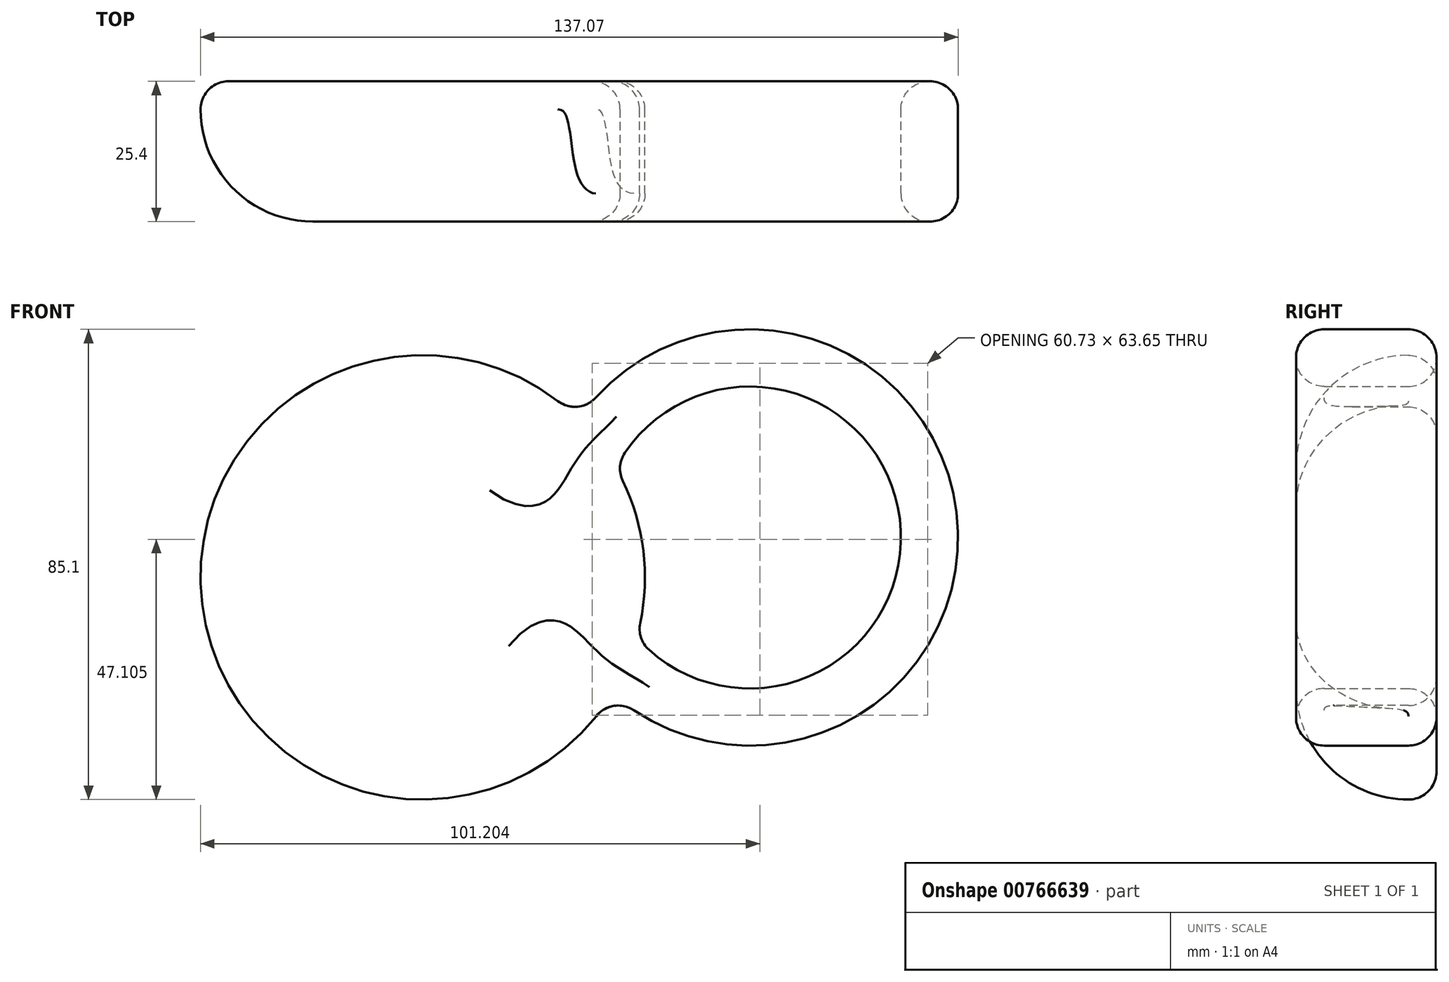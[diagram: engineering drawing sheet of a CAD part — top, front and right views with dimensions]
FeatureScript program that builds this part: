
annotation { "Feature Type Name" : "Feature", "Feature Type Description" : "" }
export const myFeature = defineFeature(function(context is Context, id is Id, definition is map)
    precondition{}
    {
        {
            var Q0;
            Q0=qCreatedBy(makeId("Front.planeOp"),FACE);
            var sketch = newSketch(context, id + "F0", { "sketchPlane" : qUnion([Q0])});
            skCircle(sketch, "E0", {"center": v(-101.84, 40.23) * mm, "radius": 40.2 * mm});
            skSolve(sketch);
        }
        {
            var Q0;
            Q0 = qSketchRegion(id + "F0", true);
            extrude(context, id + "F1", {"entities" : qUnion([Q0]), "depth" : 25.4 * mm, "offsetDistance" : 25.4 * mm});
        }
        {
            var Q0;
            Q0=qCreatedBy(makeId("Front.planeOp"),FACE);
            var sketch = newSketch(context, id + "F2", { "sketchPlane" : qUnion([Q0])});
            skCircle(sketch, "E1", {"center": v(-42.64, 47.45) * mm, "radius": 37.67 * mm});
            skCircle(sketch, "E2", {"center": v(-42.64, 47.45) * mm, "radius": 27.33 * mm});
            skSolve(sketch);
        }
        {
            var Q0;
            Q0 = qSketchRegion(id + "F2", true);
            extrude(context, id + "F3", {"entities" : qUnion([Q0]), "operationType" : NewBodyOperationType.ADD, "depth" : 25.4 * mm, "offsetDistance" : 25.4 * mm});
        }
        {
            var Q0;
            Q0=makeQuery(id+"F3.opExtrude","CAP_EDGE",EDGE,{"disambiguationData":[OSD([sQuery(id+"F2.wireOp",EDGE,"E1")])],"isStart":false});
            var Q1;
            Q1=makeQuery(id+"F3.opExtrude","CAP_EDGE",EDGE,{"disambiguationData":[OSD([sQuery(id+"F2.wireOp",EDGE,"E2")])],"isStart":false});
            fillet(context, id + "F4", {"entities" : qUnion([Q0, Q1]), "radius" : 5.08 * mm, "tangentPropagation" : true, "allowEdgeOverflow" : false});
        }
        {
            var Q0;
            {var subQ0=sQuery(id+"F2.wireOp",EDGE,"E2");var subQ2=sQuery(id+"F0.wireOp",EDGE,"E0");Q0=makeQuery(id+"F3.boolean.opBoolean","SPLIT",FACE,{"disambiguationData":[TD([makeQuery(id+"F3.opExtrude","SWEPT_FACE",FACE,{"disambiguationData":[OSD([subQ0])]})])],"derivedFrom":makeQuery(id+"F1.opExtrude","SWEPT_FACE",FACE,{"disambiguationData":[OSD([subQ2])]})});}
            var Q1;
            Q1=makeQuery(id+"F3.boolean.opBoolean","INTERSECT",EDGE,{"disambiguationData":[OD(0.0)],"derivedFrom":[makeQuery(id+"F1.opExtrude","SWEPT_FACE",FACE,{"disambiguationData":[OSD([sQuery(id+"F0.wireOp",EDGE,"E0")])]}),makeQuery(id+"F3.opExtrude","SWEPT_FACE",FACE,{"disambiguationData":[OSD([sQuery(id+"F2.wireOp",EDGE,"E1")])]})]});
            var Q2;
            Q2=makeQuery(id+"F3.boolean.opBoolean","INTERSECT",EDGE,{"disambiguationData":[OD(1.0)],"derivedFrom":[makeQuery(id+"F1.opExtrude","SWEPT_FACE",FACE,{"disambiguationData":[OSD([sQuery(id+"F0.wireOp",EDGE,"E0")])]}),makeQuery(id+"F3.opExtrude","SWEPT_FACE",FACE,{"disambiguationData":[OSD([sQuery(id+"F2.wireOp",EDGE,"E1")])]})]});
            fillet(context, id + "F5", {"entities" : qUnion([Q0, Q1, Q2]), "radius" : 5.08 * mm, "tangentPropagation" : true, "allowEdgeOverflow" : false});
        }
        {
            var Q0;
            Q0=makeQuery(id+"F3.boolean.opBoolean","MERGE",FACE,{"derivedFrom":[makeQuery(id+"F1.opExtrude","CAP_FACE",FACE,{"disambiguationData":[OSD([sQuery(id+"F0.wireOp",EDGE,"E0")])],"isStart":true}),makeQuery(id+"F3.opExtrude","CAP_FACE",FACE,{"disambiguationData":[OSD([sQuery(id+"F2.wireOp",EDGE,"E1"),sQuery(id+"F2.wireOp",EDGE,"E2")])],"isStart":true})]});
            fillet(context, id + "F6", {"entities" : qUnion([Q0]), "radius" : 5.08 * mm, "tangentPropagation" : true, "allowEdgeOverflow" : false});
        }
        {
            var Q0;
            Q0=makeQuery(id+"F3.boolean.opBoolean","MERGE",FACE,{"derivedFrom":[makeQuery(id+"F1.opExtrude","CAP_FACE",FACE,{"disambiguationData":[OSD([sQuery(id+"F0.wireOp",EDGE,"E0")])],"isStart":false}),makeQuery(id+"F3.opExtrude","CAP_FACE",FACE,{"disambiguationData":[OSD([sQuery(id+"F2.wireOp",EDGE,"E1"),sQuery(id+"F2.wireOp",EDGE,"E2")])],"isStart":false})]});
            var Q1;
            {var subQ0=sQuery(id+"F0.wireOp",EDGE,"E0");var subQ1=makeQuery(id+"F1.opExtrude","SWEPT_FACE",FACE,{"disambiguationData":[OSD([subQ0])]});var subQ2=sQuery(id+"F2.wireOp",EDGE,"E2");var subQ3=makeQuery(id+"F3.opExtrude","SWEPT_FACE",FACE,{"disambiguationData":[OSD([subQ2])]});Q1=makeQuery(id+"F5.opFillet","BLEND_EDGE",EDGE,{"blendedFrom":[makeQuery(id+"F3.boolean.opBoolean","INTERSECT",VERTEX,{"disambiguationData":[OD(0.0)],"derivedFrom":[subQ1,subQ3]}),makeQuery(id+"F3.boolean.opBoolean","SPLIT",EDGE,{"disambiguationData":[TD([subQ3])],"derivedFrom":makeQuery(id+"F1.opExtrude","CAP_EDGE",EDGE,{"disambiguationData":[OSD([subQ0])],"isStart":true})})],"blendedInto":[]});}
            var Q2;
            {var subQ0=sQuery(id+"F2.wireOp",EDGE,"E2");var subQ1=sQuery(id+"F0.wireOp",EDGE,"E0");Q2=makeQuery(id+"F5.opFillet","BLEND_EDGE",EDGE,{"blendedFrom":[makeQuery(id+"F3.boolean.opBoolean","INTERSECT",VERTEX,{"disambiguationData":[OD(0.0)],"derivedFrom":[makeQuery(id+"F1.opExtrude","SWEPT_FACE",FACE,{"disambiguationData":[OSD([subQ1])]}),makeQuery(id+"F3.opExtrude","SWEPT_FACE",FACE,{"disambiguationData":[OSD([subQ0])]})]}),makeQuery(id+"F3.boolean.opBoolean","MERGE",FACE,{"derivedFrom":[makeQuery(id+"F1.opExtrude","CAP_FACE",FACE,{"disambiguationData":[OSD([subQ1])],"isStart":true}),makeQuery(id+"F3.opExtrude","CAP_FACE",FACE,{"disambiguationData":[OSD([sQuery(id+"F2.wireOp",EDGE,"E1"),subQ0])],"isStart":true})]})],"blendedInto":[makeQuery(id+"F3.boolean.opBoolean","MERGE",FACE,{"derivedFrom":[makeQuery(id+"F1.opExtrude","CAP_FACE",FACE,{"disambiguationData":[OSD([subQ1])],"isStart":true}),makeQuery(id+"F3.opExtrude","CAP_FACE",FACE,{"disambiguationData":[OSD([sQuery(id+"F2.wireOp",EDGE,"E1"),subQ0])],"isStart":true})]})]});}
            var Q3;
            {var subQ0=makeQuery(id+"F3.opExtrude","SWEPT_FACE",FACE,{"disambiguationData":[OSD([sQuery(id+"F2.wireOp",EDGE,"E2")])]});var subQ1=makeQuery(id+"F1.opExtrude","SWEPT_FACE",FACE,{"disambiguationData":[OSD([sQuery(id+"F0.wireOp",EDGE,"E0")])]});Q3=makeQuery(id+"F5.opFillet","BLEND_EDGE",EDGE,{"blendedFrom":[makeQuery(id+"F3.boolean.opBoolean","INTERSECT",VERTEX,{"disambiguationData":[OD(0.0)],"derivedFrom":[subQ1,subQ0]}),makeQuery(id+"F3.boolean.opBoolean","INTERSECT",EDGE,{"disambiguationData":[OD(0.0)],"derivedFrom":[subQ1,subQ0]})],"blendedInto":[]});}
            var Q4;
            {var subQ0=sQuery(id+"F2.wireOp",EDGE,"E1");var subQ1=makeQuery(id+"F3.opExtrude","CAP_FACE",FACE,{"disambiguationData":[OSD([subQ0,sQuery(id+"F2.wireOp",EDGE,"E2")])],"isStart":true});var subQ2=sQuery(id+"F0.wireOp",EDGE,"E0");var subQ3=makeQuery(id+"F1.opExtrude","CAP_FACE",FACE,{"disambiguationData":[OSD([subQ2])],"isStart":true});var subQ4=makeQuery(id+"F3.opExtrude","SWEPT_FACE",FACE,{"disambiguationData":[OSD([subQ0])]});var subQ5=makeQuery(id+"F1.opExtrude","SWEPT_FACE",FACE,{"disambiguationData":[OSD([subQ2])]});Q4=makeQuery(id+"F6.opFillet","BLEND_EDGE",EDGE,{"blendedFrom":[makeQuery(id+"F3.boolean.opBoolean","SPLIT",EDGE,{"disambiguationData":[TD([subQ4])],"derivedFrom":makeQuery(id+"F1.opExtrude","CAP_EDGE",EDGE,{"disambiguationData":[OSD([subQ2])],"isStart":true})}),makeQuery(id+"F5.opFillet","BLEND_EDGE",EDGE,{"blendedFrom":[makeQuery(id+"F3.boolean.opBoolean","INTERSECT",EDGE,{"disambiguationData":[OD(0.0)],"derivedFrom":[subQ5,subQ4]}),makeQuery(id+"F3.boolean.opBoolean","MERGE",FACE,{"derivedFrom":[subQ3,subQ1]})],"blendedInto":[makeQuery(id+"F3.boolean.opBoolean","MERGE",FACE,{"derivedFrom":[subQ3,subQ1]})]})],"blendedInto":[]});}
            var Q5;
            {var subQ0=sQuery(id+"F2.wireOp",EDGE,"E2");Q5=makeQuery(id+"F5.opFillet","BLEND_EDGE",EDGE,{"blendedFrom":[makeQuery(id+"F3.boolean.opBoolean","INTERSECT",VERTEX,{"disambiguationData":[OD(0.0)],"derivedFrom":[makeQuery(id+"F1.opExtrude","SWEPT_FACE",FACE,{"disambiguationData":[OSD([sQuery(id+"F0.wireOp",EDGE,"E0")])]}),makeQuery(id+"F3.opExtrude","SWEPT_FACE",FACE,{"disambiguationData":[OSD([subQ0])]})]}),makeQuery(id+"F3.opExtrude","CAP_EDGE",EDGE,{"disambiguationData":[OSD([subQ0])],"isStart":true})],"blendedInto":[]});}
            var Q6;
            {var subQ0=makeQuery(id+"F3.opExtrude","SWEPT_FACE",FACE,{"disambiguationData":[OSD([sQuery(id+"F2.wireOp",EDGE,"E1")])]});Q6=makeQuery(id+"F5.opFillet","BLEND_EDGE",EDGE,{"blendedFrom":[makeQuery(id+"F3.boolean.opBoolean","INTERSECT",EDGE,{"disambiguationData":[OD(1.0)],"derivedFrom":[makeQuery(id+"F1.opExtrude","SWEPT_FACE",FACE,{"disambiguationData":[OSD([sQuery(id+"F0.wireOp",EDGE,"E0")])]}),subQ0]}),subQ0],"blendedInto":[subQ0]});}
            var Q7;
            {var subQ0=makeQuery(id+"F3.opExtrude","SWEPT_FACE",FACE,{"disambiguationData":[OSD([sQuery(id+"F2.wireOp",EDGE,"E1")])]});Q7=makeQuery(id+"F5.opFillet","BLEND_EDGE",EDGE,{"blendedFrom":[makeQuery(id+"F3.boolean.opBoolean","INTERSECT",EDGE,{"disambiguationData":[OD(0.0)],"derivedFrom":[makeQuery(id+"F1.opExtrude","SWEPT_FACE",FACE,{"disambiguationData":[OSD([sQuery(id+"F0.wireOp",EDGE,"E0")])]}),subQ0]}),subQ0],"blendedInto":[subQ0]});}
            var Q8;
            {var subQ0=sQuery(id+"F2.wireOp",EDGE,"E2");var subQ3=sQuery(id+"F0.wireOp",EDGE,"E0");var subQ5=makeQuery(id+"F3.opExtrude","SWEPT_FACE",FACE,{"disambiguationData":[OSD([subQ0])]});var subQ6=makeQuery(id+"F1.opExtrude","SWEPT_FACE",FACE,{"disambiguationData":[OSD([subQ3])]});Q8=makeQuery(id+"F5.opFillet","BLEND_EDGE",EDGE,{"blendedFrom":[makeQuery(id+"F3.boolean.opBoolean","SPLIT",EDGE,{"disambiguationData":[TD([subQ5])],"derivedFrom":makeQuery(id+"F1.opExtrude","CAP_EDGE",EDGE,{"disambiguationData":[OSD([subQ3])],"isStart":true})}),makeQuery(id+"F3.boolean.opBoolean","SPLIT",FACE,{"disambiguationData":[TD([subQ5])],"derivedFrom":subQ6})],"blendedInto":[makeQuery(id+"F3.boolean.opBoolean","SPLIT",FACE,{"disambiguationData":[TD([subQ5])],"derivedFrom":subQ6})]});}
            var Q9;
            {var subQ0=sQuery(id+"F2.wireOp",EDGE,"E2");var subQ1=makeQuery(id+"F3.opExtrude","CAP_FACE",FACE,{"disambiguationData":[OSD([sQuery(id+"F2.wireOp",EDGE,"E1"),subQ0])],"isStart":true});var subQ2=sQuery(id+"F0.wireOp",EDGE,"E0");var subQ3=makeQuery(id+"F1.opExtrude","CAP_FACE",FACE,{"disambiguationData":[OSD([subQ2])],"isStart":true});Q9=makeQuery(id+"F5.opFillet","BLEND_EDGE",EDGE,{"blendedFrom":[makeQuery(id+"F3.boolean.opBoolean","SPLIT",EDGE,{"disambiguationData":[TD([makeQuery(id+"F3.opExtrude","SWEPT_FACE",FACE,{"disambiguationData":[OSD([subQ0])]})])],"derivedFrom":makeQuery(id+"F1.opExtrude","CAP_EDGE",EDGE,{"disambiguationData":[OSD([subQ2])],"isStart":true})}),makeQuery(id+"F3.boolean.opBoolean","MERGE",FACE,{"derivedFrom":[subQ3,subQ1]})],"blendedInto":[makeQuery(id+"F3.boolean.opBoolean","MERGE",FACE,{"derivedFrom":[subQ3,subQ1]})]});}
            var Q10;
            {var subQ0=sQuery(id+"F2.wireOp",EDGE,"E2");var subQ1=makeQuery(id+"F3.opExtrude","CAP_FACE",FACE,{"disambiguationData":[OSD([sQuery(id+"F2.wireOp",EDGE,"E1"),subQ0])],"isStart":false});var subQ2=sQuery(id+"F0.wireOp",EDGE,"E0");var subQ3=makeQuery(id+"F1.opExtrude","CAP_FACE",FACE,{"disambiguationData":[OSD([subQ2])],"isStart":false});Q10=makeQuery(id+"F5.opFillet","BLEND_EDGE",EDGE,{"blendedFrom":[makeQuery(id+"F3.boolean.opBoolean","SPLIT",EDGE,{"disambiguationData":[TD([makeQuery(id+"F3.opExtrude","SWEPT_FACE",FACE,{"disambiguationData":[OSD([subQ0])]})])],"derivedFrom":makeQuery(id+"F1.opExtrude","CAP_EDGE",EDGE,{"disambiguationData":[OSD([subQ2])],"isStart":false})}),makeQuery(id+"F3.boolean.opBoolean","MERGE",FACE,{"derivedFrom":[subQ3,subQ1]})],"blendedInto":[makeQuery(id+"F3.boolean.opBoolean","MERGE",FACE,{"derivedFrom":[subQ3,subQ1]})]});}
            var Q11;
            {var subQ0=sQuery(id+"F2.wireOp",EDGE,"E2");var subQ2=sQuery(id+"F0.wireOp",EDGE,"E0");Q11=makeQuery(id+"F5.opFillet","BLEND_EDGE",EDGE,{"blendedFrom":[makeQuery(id+"F4.opFillet","BLEND_EDGE",EDGE,{"disambiguationData":[OD(1.0)],"blendedFrom":[makeQuery(id+"F3.opExtrude","CAP_EDGE",EDGE,{"disambiguationData":[OSD([subQ0])],"isStart":false}),makeQuery(id+"F3.boolean.opBoolean","SPLIT",FACE,{"disambiguationData":[TD([makeQuery(id+"F3.opExtrude","SWEPT_FACE",FACE,{"disambiguationData":[OSD([subQ0])]})])],"derivedFrom":makeQuery(id+"F1.opExtrude","SWEPT_FACE",FACE,{"disambiguationData":[OSD([subQ2])]})})],"blendedInto":[makeQuery(id+"F3.boolean.opBoolean","SPLIT",FACE,{"disambiguationData":[TD([makeQuery(id+"F3.opExtrude","SWEPT_FACE",FACE,{"disambiguationData":[OSD([subQ0])]})])],"derivedFrom":makeQuery(id+"F1.opExtrude","SWEPT_FACE",FACE,{"disambiguationData":[OSD([subQ2])]})})]}),makeQuery(id+"F4.opFillet","BLEND_FACE",FACE,{"disambiguationData":[OSD([subQ0])]})],"blendedInto":[makeQuery(id+"F4.opFillet","BLEND_FACE",FACE,{"disambiguationData":[OSD([subQ0])]})]});}
            var Q12;
            {var subQ0=sQuery(id+"F2.wireOp",EDGE,"E2");var subQ3=sQuery(id+"F0.wireOp",EDGE,"E0");var subQ5=makeQuery(id+"F3.opExtrude","SWEPT_FACE",FACE,{"disambiguationData":[OSD([subQ0])]});var subQ6=makeQuery(id+"F1.opExtrude","SWEPT_FACE",FACE,{"disambiguationData":[OSD([subQ3])]});Q12=makeQuery(id+"F5.opFillet","BLEND_EDGE",EDGE,{"blendedFrom":[makeQuery(id+"F3.boolean.opBoolean","SPLIT",EDGE,{"disambiguationData":[TD([subQ5])],"derivedFrom":makeQuery(id+"F1.opExtrude","CAP_EDGE",EDGE,{"disambiguationData":[OSD([subQ3])],"isStart":false})}),makeQuery(id+"F3.boolean.opBoolean","SPLIT",FACE,{"disambiguationData":[TD([subQ5])],"derivedFrom":subQ6})],"blendedInto":[makeQuery(id+"F3.boolean.opBoolean","SPLIT",FACE,{"disambiguationData":[TD([subQ5])],"derivedFrom":subQ6})]});}
            var Q13;
            {var subQ0=sQuery(id+"F2.wireOp",EDGE,"E2");var subQ1=sQuery(id+"F2.wireOp",EDGE,"E1");var subQ2=makeQuery(id+"F3.opExtrude","CAP_FACE",FACE,{"disambiguationData":[OSD([subQ1,subQ0])],"isStart":false});var subQ3=sQuery(id+"F0.wireOp",EDGE,"E0");var subQ4=makeQuery(id+"F1.opExtrude","CAP_FACE",FACE,{"disambiguationData":[OSD([subQ3])],"isStart":false});Q13=makeQuery(id+"F5.opFillet","BLEND_EDGE",EDGE,{"blendedFrom":[makeQuery(id+"F4.opFillet","BLEND_EDGE",EDGE,{"disambiguationData":[OD(1.0)],"blendedFrom":[makeQuery(id+"F3.opExtrude","CAP_EDGE",EDGE,{"disambiguationData":[OSD([subQ0])],"isStart":false}),makeQuery(id+"F3.boolean.opBoolean","SPLIT",FACE,{"disambiguationData":[TD([makeQuery(id+"F3.opExtrude","SWEPT_FACE",FACE,{"disambiguationData":[OSD([subQ0])]})])],"derivedFrom":makeQuery(id+"F1.opExtrude","SWEPT_FACE",FACE,{"disambiguationData":[OSD([subQ3])]})})],"blendedInto":[makeQuery(id+"F3.boolean.opBoolean","SPLIT",FACE,{"disambiguationData":[TD([makeQuery(id+"F3.opExtrude","SWEPT_FACE",FACE,{"disambiguationData":[OSD([subQ0])]})])],"derivedFrom":makeQuery(id+"F1.opExtrude","SWEPT_FACE",FACE,{"disambiguationData":[OSD([subQ3])]})})]}),makeQuery(id+"F3.boolean.opBoolean","MERGE",FACE,{"derivedFrom":[subQ4,subQ2]})],"blendedInto":[makeQuery(id+"F3.boolean.opBoolean","MERGE",FACE,{"derivedFrom":[subQ4,subQ2]})]});}
            var Q14;
            {var subQ1=sQuery(id+"F2.wireOp",EDGE,"E1");var subQ2=sQuery(id+"F0.wireOp",EDGE,"E0");var subQ3=makeQuery(id+"F3.opExtrude","SWEPT_FACE",FACE,{"disambiguationData":[OSD([subQ1])]});var subQ4=makeQuery(id+"F1.opExtrude","SWEPT_FACE",FACE,{"disambiguationData":[OSD([subQ2])]});Q14=makeQuery(id+"F5.opFillet","BLEND_EDGE",EDGE,{"blendedFrom":[makeQuery(id+"F3.boolean.opBoolean","INTERSECT",EDGE,{"disambiguationData":[OD(1.0)],"derivedFrom":[subQ4,subQ3]}),makeQuery(id+"F4.opFillet","BLEND_EDGE",EDGE,{"disambiguationData":[OD(1.0)],"blendedFrom":[makeQuery(id+"F3.opExtrude","CAP_EDGE",EDGE,{"disambiguationData":[OSD([subQ1])],"isStart":false}),makeQuery(id+"F3.boolean.opBoolean","SPLIT",FACE,{"disambiguationData":[TD([subQ3])],"derivedFrom":subQ4})],"blendedInto":[makeQuery(id+"F3.boolean.opBoolean","SPLIT",FACE,{"disambiguationData":[TD([subQ3])],"derivedFrom":subQ4})]})],"blendedInto":[]});}
            var Q15;
            {var subQ0=sQuery(id+"F2.wireOp",EDGE,"E1");var subQ1=sQuery(id+"F0.wireOp",EDGE,"E0");Q15=makeQuery(id+"F6.opFillet","BLEND_EDGE",EDGE,{"blendedFrom":[makeQuery(id+"F3.opExtrude","CAP_EDGE",EDGE,{"disambiguationData":[OSD([subQ0])],"isStart":true}),makeQuery(id+"F5.opFillet","BLEND_EDGE",EDGE,{"blendedFrom":[makeQuery(id+"F3.boolean.opBoolean","INTERSECT",EDGE,{"disambiguationData":[OD(1.0)],"derivedFrom":[makeQuery(id+"F1.opExtrude","SWEPT_FACE",FACE,{"disambiguationData":[OSD([subQ1])]}),makeQuery(id+"F3.opExtrude","SWEPT_FACE",FACE,{"disambiguationData":[OSD([subQ0])]})]}),makeQuery(id+"F3.boolean.opBoolean","MERGE",FACE,{"derivedFrom":[makeQuery(id+"F1.opExtrude","CAP_FACE",FACE,{"disambiguationData":[OSD([subQ1])],"isStart":true}),makeQuery(id+"F3.opExtrude","CAP_FACE",FACE,{"disambiguationData":[OSD([subQ0,sQuery(id+"F2.wireOp",EDGE,"E2")])],"isStart":true})]})],"blendedInto":[makeQuery(id+"F3.boolean.opBoolean","MERGE",FACE,{"derivedFrom":[makeQuery(id+"F1.opExtrude","CAP_FACE",FACE,{"disambiguationData":[OSD([subQ1])],"isStart":true}),makeQuery(id+"F3.opExtrude","CAP_FACE",FACE,{"disambiguationData":[OSD([subQ0,sQuery(id+"F2.wireOp",EDGE,"E2")])],"isStart":true})]})]})],"blendedInto":[]});}
            var Q16;
            {var subQ0=sQuery(id+"F2.wireOp",EDGE,"E2");var subQ2=sQuery(id+"F0.wireOp",EDGE,"E0");var subQ3=makeQuery(id+"F3.opExtrude","SWEPT_FACE",FACE,{"disambiguationData":[OSD([subQ0])]});var subQ4=makeQuery(id+"F1.opExtrude","SWEPT_FACE",FACE,{"disambiguationData":[OSD([subQ2])]});Q16=makeQuery(id+"F5.opFillet","BLEND_EDGE",EDGE,{"blendedFrom":[makeQuery(id+"F3.boolean.opBoolean","INTERSECT",EDGE,{"disambiguationData":[OD(1.0)],"derivedFrom":[subQ4,subQ3]}),makeQuery(id+"F4.opFillet","BLEND_EDGE",EDGE,{"disambiguationData":[OD(1.0)],"blendedFrom":[makeQuery(id+"F3.opExtrude","CAP_EDGE",EDGE,{"disambiguationData":[OSD([subQ0])],"isStart":false}),makeQuery(id+"F3.boolean.opBoolean","SPLIT",FACE,{"disambiguationData":[TD([subQ3])],"derivedFrom":subQ4})],"blendedInto":[makeQuery(id+"F3.boolean.opBoolean","SPLIT",FACE,{"disambiguationData":[TD([subQ3])],"derivedFrom":subQ4})]})],"blendedInto":[]});}
            var Q17;
            {var subQ0=makeQuery(id+"F3.opExtrude","SWEPT_FACE",FACE,{"disambiguationData":[OSD([sQuery(id+"F2.wireOp",EDGE,"E2")])]});Q17=makeQuery(id+"F5.opFillet","BLEND_EDGE",EDGE,{"blendedFrom":[makeQuery(id+"F3.boolean.opBoolean","INTERSECT",EDGE,{"disambiguationData":[OD(1.0)],"derivedFrom":[makeQuery(id+"F1.opExtrude","SWEPT_FACE",FACE,{"disambiguationData":[OSD([sQuery(id+"F0.wireOp",EDGE,"E0")])]}),subQ0]}),subQ0],"blendedInto":[subQ0]});}
            var Q18;
            {var subQ1=sQuery(id+"F2.wireOp",EDGE,"E1");var subQ2=sQuery(id+"F0.wireOp",EDGE,"E0");var subQ3=makeQuery(id+"F3.opExtrude","SWEPT_FACE",FACE,{"disambiguationData":[OSD([subQ1])]});var subQ4=makeQuery(id+"F1.opExtrude","SWEPT_FACE",FACE,{"disambiguationData":[OSD([subQ2])]});Q18=makeQuery(id+"F5.opFillet","BLEND_EDGE",EDGE,{"blendedFrom":[makeQuery(id+"F3.boolean.opBoolean","INTERSECT",EDGE,{"disambiguationData":[OD(0.0)],"derivedFrom":[subQ4,subQ3]}),makeQuery(id+"F4.opFillet","BLEND_EDGE",EDGE,{"disambiguationData":[OD(0.0)],"blendedFrom":[makeQuery(id+"F3.opExtrude","CAP_EDGE",EDGE,{"disambiguationData":[OSD([subQ1])],"isStart":false}),makeQuery(id+"F3.boolean.opBoolean","SPLIT",FACE,{"disambiguationData":[TD([subQ3])],"derivedFrom":subQ4})],"blendedInto":[makeQuery(id+"F3.boolean.opBoolean","SPLIT",FACE,{"disambiguationData":[TD([subQ3])],"derivedFrom":subQ4})]})],"blendedInto":[]});}
            var Q19;
            {var subQ0=sQuery(id+"F2.wireOp",EDGE,"E2");var subQ2=sQuery(id+"F0.wireOp",EDGE,"E0");var subQ3=makeQuery(id+"F3.opExtrude","SWEPT_FACE",FACE,{"disambiguationData":[OSD([subQ0])]});var subQ4=makeQuery(id+"F1.opExtrude","SWEPT_FACE",FACE,{"disambiguationData":[OSD([subQ2])]});Q19=makeQuery(id+"F5.opFillet","BLEND_EDGE",EDGE,{"blendedFrom":[makeQuery(id+"F3.boolean.opBoolean","INTERSECT",EDGE,{"disambiguationData":[OD(1.0)],"derivedFrom":[subQ4,subQ3]}),makeQuery(id+"F3.boolean.opBoolean","SPLIT",FACE,{"disambiguationData":[TD([subQ3])],"derivedFrom":subQ4})],"blendedInto":[makeQuery(id+"F3.boolean.opBoolean","SPLIT",FACE,{"disambiguationData":[TD([subQ3])],"derivedFrom":subQ4})]});}
            var Q20;
            {var subQ1=sQuery(id+"F2.wireOp",EDGE,"E1");var subQ2=sQuery(id+"F0.wireOp",EDGE,"E0");var subQ3=makeQuery(id+"F3.opExtrude","SWEPT_FACE",FACE,{"disambiguationData":[OSD([subQ1])]});var subQ4=makeQuery(id+"F1.opExtrude","SWEPT_FACE",FACE,{"disambiguationData":[OSD([subQ2])]});Q20=makeQuery(id+"F5.opFillet","BLEND_EDGE",EDGE,{"blendedFrom":[makeQuery(id+"F3.boolean.opBoolean","INTERSECT",EDGE,{"disambiguationData":[OD(1.0)],"derivedFrom":[subQ4,subQ3]}),makeQuery(id+"F3.boolean.opBoolean","SPLIT",FACE,{"disambiguationData":[TD([subQ3])],"derivedFrom":subQ4})],"blendedInto":[makeQuery(id+"F3.boolean.opBoolean","SPLIT",FACE,{"disambiguationData":[TD([subQ3])],"derivedFrom":subQ4})]});}
            var Q21;
            {var subQ0=sQuery(id+"F2.wireOp",EDGE,"E1");var subQ2=sQuery(id+"F0.wireOp",EDGE,"E0");Q21=makeQuery(id+"F5.opFillet","BLEND_EDGE",EDGE,{"blendedFrom":[makeQuery(id+"F4.opFillet","BLEND_EDGE",EDGE,{"disambiguationData":[OD(0.0)],"blendedFrom":[makeQuery(id+"F3.opExtrude","CAP_EDGE",EDGE,{"disambiguationData":[OSD([subQ0])],"isStart":false}),makeQuery(id+"F3.boolean.opBoolean","SPLIT",FACE,{"disambiguationData":[TD([makeQuery(id+"F3.opExtrude","SWEPT_FACE",FACE,{"disambiguationData":[OSD([subQ0])]})])],"derivedFrom":makeQuery(id+"F1.opExtrude","SWEPT_FACE",FACE,{"disambiguationData":[OSD([subQ2])]})})],"blendedInto":[makeQuery(id+"F3.boolean.opBoolean","SPLIT",FACE,{"disambiguationData":[TD([makeQuery(id+"F3.opExtrude","SWEPT_FACE",FACE,{"disambiguationData":[OSD([subQ0])]})])],"derivedFrom":makeQuery(id+"F1.opExtrude","SWEPT_FACE",FACE,{"disambiguationData":[OSD([subQ2])]})})]}),makeQuery(id+"F4.opFillet","BLEND_FACE",FACE,{"disambiguationData":[OSD([subQ0])]})],"blendedInto":[makeQuery(id+"F4.opFillet","BLEND_FACE",FACE,{"disambiguationData":[OSD([subQ0])]})]});}
            var Q22;
            {var subQ0=sQuery(id+"F2.wireOp",EDGE,"E1");var subQ1=sQuery(id+"F0.wireOp",EDGE,"E0");Q22=makeQuery(id+"F6.opFillet","BLEND_EDGE",EDGE,{"blendedFrom":[makeQuery(id+"F3.opExtrude","CAP_EDGE",EDGE,{"disambiguationData":[OSD([subQ0])],"isStart":true}),makeQuery(id+"F5.opFillet","BLEND_EDGE",EDGE,{"blendedFrom":[makeQuery(id+"F3.boolean.opBoolean","INTERSECT",EDGE,{"disambiguationData":[OD(0.0)],"derivedFrom":[makeQuery(id+"F1.opExtrude","SWEPT_FACE",FACE,{"disambiguationData":[OSD([subQ1])]}),makeQuery(id+"F3.opExtrude","SWEPT_FACE",FACE,{"disambiguationData":[OSD([subQ0])]})]}),makeQuery(id+"F3.boolean.opBoolean","MERGE",FACE,{"derivedFrom":[makeQuery(id+"F1.opExtrude","CAP_FACE",FACE,{"disambiguationData":[OSD([subQ1])],"isStart":true}),makeQuery(id+"F3.opExtrude","CAP_FACE",FACE,{"disambiguationData":[OSD([subQ0,sQuery(id+"F2.wireOp",EDGE,"E2")])],"isStart":true})]})],"blendedInto":[makeQuery(id+"F3.boolean.opBoolean","MERGE",FACE,{"derivedFrom":[makeQuery(id+"F1.opExtrude","CAP_FACE",FACE,{"disambiguationData":[OSD([subQ1])],"isStart":true}),makeQuery(id+"F3.opExtrude","CAP_FACE",FACE,{"disambiguationData":[OSD([subQ0,sQuery(id+"F2.wireOp",EDGE,"E2")])],"isStart":true})]})]})],"blendedInto":[]});}
            var Q23;
            {var subQ0=sQuery(id+"F2.wireOp",EDGE,"E2");var subQ1=sQuery(id+"F2.wireOp",EDGE,"E1");var subQ2=makeQuery(id+"F3.opExtrude","CAP_FACE",FACE,{"disambiguationData":[OSD([subQ1,subQ0])],"isStart":false});var subQ3=sQuery(id+"F0.wireOp",EDGE,"E0");var subQ4=makeQuery(id+"F1.opExtrude","CAP_FACE",FACE,{"disambiguationData":[OSD([subQ3])],"isStart":false});Q23=makeQuery(id+"F5.opFillet","BLEND_EDGE",EDGE,{"blendedFrom":[makeQuery(id+"F4.opFillet","BLEND_EDGE",EDGE,{"disambiguationData":[OD(0.0)],"blendedFrom":[makeQuery(id+"F3.opExtrude","CAP_EDGE",EDGE,{"disambiguationData":[OSD([subQ1])],"isStart":false}),makeQuery(id+"F3.boolean.opBoolean","SPLIT",FACE,{"disambiguationData":[TD([makeQuery(id+"F3.opExtrude","SWEPT_FACE",FACE,{"disambiguationData":[OSD([subQ1])]})])],"derivedFrom":makeQuery(id+"F1.opExtrude","SWEPT_FACE",FACE,{"disambiguationData":[OSD([subQ3])]})})],"blendedInto":[makeQuery(id+"F3.boolean.opBoolean","SPLIT",FACE,{"disambiguationData":[TD([makeQuery(id+"F3.opExtrude","SWEPT_FACE",FACE,{"disambiguationData":[OSD([subQ1])]})])],"derivedFrom":makeQuery(id+"F1.opExtrude","SWEPT_FACE",FACE,{"disambiguationData":[OSD([subQ3])]})})]}),makeQuery(id+"F3.boolean.opBoolean","MERGE",FACE,{"derivedFrom":[subQ4,subQ2]})],"blendedInto":[makeQuery(id+"F3.boolean.opBoolean","MERGE",FACE,{"derivedFrom":[subQ4,subQ2]})]});}
            var Q24;
            {var subQ0=sQuery(id+"F2.wireOp",EDGE,"E2");var subQ2=sQuery(id+"F0.wireOp",EDGE,"E0");var subQ3=makeQuery(id+"F3.opExtrude","SWEPT_FACE",FACE,{"disambiguationData":[OSD([subQ0])]});var subQ4=makeQuery(id+"F1.opExtrude","SWEPT_FACE",FACE,{"disambiguationData":[OSD([subQ2])]});Q24=makeQuery(id+"F5.opFillet","BLEND_EDGE",EDGE,{"blendedFrom":[makeQuery(id+"F3.boolean.opBoolean","INTERSECT",EDGE,{"disambiguationData":[OD(0.0)],"derivedFrom":[subQ4,subQ3]}),makeQuery(id+"F4.opFillet","BLEND_EDGE",EDGE,{"disambiguationData":[OD(0.0)],"blendedFrom":[makeQuery(id+"F3.opExtrude","CAP_EDGE",EDGE,{"disambiguationData":[OSD([subQ0])],"isStart":false}),makeQuery(id+"F3.boolean.opBoolean","SPLIT",FACE,{"disambiguationData":[TD([subQ3])],"derivedFrom":subQ4})],"blendedInto":[makeQuery(id+"F3.boolean.opBoolean","SPLIT",FACE,{"disambiguationData":[TD([subQ3])],"derivedFrom":subQ4})]})],"blendedInto":[]});}
            var Q25;
            {var subQ1=sQuery(id+"F2.wireOp",EDGE,"E1");var subQ2=sQuery(id+"F0.wireOp",EDGE,"E0");var subQ3=makeQuery(id+"F3.boolean.opBoolean","SPLIT",FACE,{"disambiguationData":[TD([makeQuery(id+"F3.opExtrude","SWEPT_FACE",FACE,{"disambiguationData":[OSD([subQ1])]})])],"derivedFrom":makeQuery(id+"F1.opExtrude","SWEPT_FACE",FACE,{"disambiguationData":[OSD([subQ2])]})});Q25=makeQuery(id+"F5.opFillet","BLEND_EDGE",EDGE,{"blendedFrom":[makeQuery(id+"F4.opFillet","BLEND_EDGE",EDGE,{"disambiguationData":[OD(0.0)],"blendedFrom":[makeQuery(id+"F3.opExtrude","CAP_EDGE",EDGE,{"disambiguationData":[OSD([subQ1])],"isStart":false}),subQ3],"blendedInto":[subQ3]}),subQ3],"blendedInto":[subQ3]});}
            var Q26;
            {var subQ0=makeQuery(id+"F3.opExtrude","SWEPT_FACE",FACE,{"disambiguationData":[OSD([sQuery(id+"F2.wireOp",EDGE,"E2")])]});Q26=makeQuery(id+"F5.opFillet","BLEND_EDGE",EDGE,{"blendedFrom":[makeQuery(id+"F3.boolean.opBoolean","INTERSECT",EDGE,{"disambiguationData":[OD(0.0)],"derivedFrom":[makeQuery(id+"F1.opExtrude","SWEPT_FACE",FACE,{"disambiguationData":[OSD([sQuery(id+"F0.wireOp",EDGE,"E0")])]}),subQ0]}),subQ0],"blendedInto":[subQ0]});}
            var Q27;
            {var subQ0=sQuery(id+"F2.wireOp",EDGE,"E1");var subQ2=sQuery(id+"F0.wireOp",EDGE,"E0");Q27=makeQuery(id+"F5.opFillet","BLEND_EDGE",EDGE,{"blendedFrom":[makeQuery(id+"F4.opFillet","BLEND_EDGE",EDGE,{"disambiguationData":[OD(1.0)],"blendedFrom":[makeQuery(id+"F3.opExtrude","CAP_EDGE",EDGE,{"disambiguationData":[OSD([subQ0])],"isStart":false}),makeQuery(id+"F3.boolean.opBoolean","SPLIT",FACE,{"disambiguationData":[TD([makeQuery(id+"F3.opExtrude","SWEPT_FACE",FACE,{"disambiguationData":[OSD([subQ0])]})])],"derivedFrom":makeQuery(id+"F1.opExtrude","SWEPT_FACE",FACE,{"disambiguationData":[OSD([subQ2])]})})],"blendedInto":[makeQuery(id+"F3.boolean.opBoolean","SPLIT",FACE,{"disambiguationData":[TD([makeQuery(id+"F3.opExtrude","SWEPT_FACE",FACE,{"disambiguationData":[OSD([subQ0])]})])],"derivedFrom":makeQuery(id+"F1.opExtrude","SWEPT_FACE",FACE,{"disambiguationData":[OSD([subQ2])]})})]}),makeQuery(id+"F4.opFillet","BLEND_FACE",FACE,{"disambiguationData":[OSD([subQ0])]})],"blendedInto":[makeQuery(id+"F4.opFillet","BLEND_FACE",FACE,{"disambiguationData":[OSD([subQ0])]})]});}
            var Q28;
            {var subQ0=sQuery(id+"F2.wireOp",EDGE,"E2");var subQ2=sQuery(id+"F0.wireOp",EDGE,"E0");var subQ3=makeQuery(id+"F3.opExtrude","SWEPT_FACE",FACE,{"disambiguationData":[OSD([subQ0])]});var subQ4=makeQuery(id+"F1.opExtrude","SWEPT_FACE",FACE,{"disambiguationData":[OSD([subQ2])]});Q28=makeQuery(id+"F5.opFillet","BLEND_EDGE",EDGE,{"blendedFrom":[makeQuery(id+"F3.boolean.opBoolean","INTERSECT",EDGE,{"disambiguationData":[OD(0.0)],"derivedFrom":[subQ4,subQ3]}),makeQuery(id+"F3.boolean.opBoolean","SPLIT",FACE,{"disambiguationData":[TD([subQ3])],"derivedFrom":subQ4})],"blendedInto":[makeQuery(id+"F3.boolean.opBoolean","SPLIT",FACE,{"disambiguationData":[TD([subQ3])],"derivedFrom":subQ4})]});}
            var Q29;
            {var subQ0=sQuery(id+"F2.wireOp",EDGE,"E2");var subQ1=sQuery(id+"F2.wireOp",EDGE,"E1");var subQ2=makeQuery(id+"F3.opExtrude","CAP_FACE",FACE,{"disambiguationData":[OSD([subQ1,subQ0])],"isStart":false});var subQ3=sQuery(id+"F0.wireOp",EDGE,"E0");var subQ4=makeQuery(id+"F1.opExtrude","CAP_FACE",FACE,{"disambiguationData":[OSD([subQ3])],"isStart":false});Q29=makeQuery(id+"F5.opFillet","BLEND_EDGE",EDGE,{"blendedFrom":[makeQuery(id+"F4.opFillet","BLEND_EDGE",EDGE,{"disambiguationData":[OD(1.0)],"blendedFrom":[makeQuery(id+"F3.opExtrude","CAP_EDGE",EDGE,{"disambiguationData":[OSD([subQ1])],"isStart":false}),makeQuery(id+"F3.boolean.opBoolean","SPLIT",FACE,{"disambiguationData":[TD([makeQuery(id+"F3.opExtrude","SWEPT_FACE",FACE,{"disambiguationData":[OSD([subQ1])]})])],"derivedFrom":makeQuery(id+"F1.opExtrude","SWEPT_FACE",FACE,{"disambiguationData":[OSD([subQ3])]})})],"blendedInto":[makeQuery(id+"F3.boolean.opBoolean","SPLIT",FACE,{"disambiguationData":[TD([makeQuery(id+"F3.opExtrude","SWEPT_FACE",FACE,{"disambiguationData":[OSD([subQ1])]})])],"derivedFrom":makeQuery(id+"F1.opExtrude","SWEPT_FACE",FACE,{"disambiguationData":[OSD([subQ3])]})})]}),makeQuery(id+"F3.boolean.opBoolean","MERGE",FACE,{"derivedFrom":[subQ4,subQ2]})],"blendedInto":[makeQuery(id+"F3.boolean.opBoolean","MERGE",FACE,{"derivedFrom":[subQ4,subQ2]})]});}
            var Q30;
            {var subQ1=sQuery(id+"F2.wireOp",EDGE,"E1");var subQ2=sQuery(id+"F0.wireOp",EDGE,"E0");var subQ3=makeQuery(id+"F3.boolean.opBoolean","SPLIT",FACE,{"disambiguationData":[TD([makeQuery(id+"F3.opExtrude","SWEPT_FACE",FACE,{"disambiguationData":[OSD([subQ1])]})])],"derivedFrom":makeQuery(id+"F1.opExtrude","SWEPT_FACE",FACE,{"disambiguationData":[OSD([subQ2])]})});Q30=makeQuery(id+"F5.opFillet","BLEND_EDGE",EDGE,{"blendedFrom":[makeQuery(id+"F4.opFillet","BLEND_EDGE",EDGE,{"disambiguationData":[OD(1.0)],"blendedFrom":[makeQuery(id+"F3.opExtrude","CAP_EDGE",EDGE,{"disambiguationData":[OSD([subQ1])],"isStart":false}),subQ3],"blendedInto":[subQ3]}),subQ3],"blendedInto":[subQ3]});}
            var Q31;
            {var subQ0=sQuery(id+"F2.wireOp",EDGE,"E2");var subQ3=sQuery(id+"F0.wireOp",EDGE,"E0");var subQ5=makeQuery(id+"F3.opExtrude","SWEPT_FACE",FACE,{"disambiguationData":[OSD([subQ0])]});var subQ6=makeQuery(id+"F1.opExtrude","SWEPT_FACE",FACE,{"disambiguationData":[OSD([subQ3])]});Q31=makeQuery(id+"F5.opFillet","BLEND_EDGE",EDGE,{"blendedFrom":[makeQuery(id+"F3.boolean.opBoolean","SPLIT",EDGE,{"disambiguationData":[TD([subQ5])],"derivedFrom":makeQuery(id+"F1.opExtrude","CAP_EDGE",EDGE,{"disambiguationData":[OSD([subQ3])],"isStart":false})}),makeQuery(id+"F4.opFillet","BLEND_EDGE",EDGE,{"disambiguationData":[OD(0.0)],"blendedFrom":[makeQuery(id+"F3.opExtrude","CAP_EDGE",EDGE,{"disambiguationData":[OSD([subQ0])],"isStart":false}),makeQuery(id+"F3.boolean.opBoolean","SPLIT",FACE,{"disambiguationData":[TD([subQ5])],"derivedFrom":subQ6})],"blendedInto":[makeQuery(id+"F3.boolean.opBoolean","SPLIT",FACE,{"disambiguationData":[TD([subQ5])],"derivedFrom":subQ6})]})],"blendedInto":[]});}
            var Q32;
            {var subQ0=sQuery(id+"F2.wireOp",EDGE,"E2");var subQ2=sQuery(id+"F0.wireOp",EDGE,"E0");Q32=makeQuery(id+"F5.opFillet","BLEND_EDGE",EDGE,{"blendedFrom":[makeQuery(id+"F4.opFillet","BLEND_EDGE",EDGE,{"disambiguationData":[OD(0.0)],"blendedFrom":[makeQuery(id+"F3.opExtrude","CAP_EDGE",EDGE,{"disambiguationData":[OSD([subQ0])],"isStart":false}),makeQuery(id+"F3.boolean.opBoolean","SPLIT",FACE,{"disambiguationData":[TD([makeQuery(id+"F3.opExtrude","SWEPT_FACE",FACE,{"disambiguationData":[OSD([subQ0])]})])],"derivedFrom":makeQuery(id+"F1.opExtrude","SWEPT_FACE",FACE,{"disambiguationData":[OSD([subQ2])]})})],"blendedInto":[makeQuery(id+"F3.boolean.opBoolean","SPLIT",FACE,{"disambiguationData":[TD([makeQuery(id+"F3.opExtrude","SWEPT_FACE",FACE,{"disambiguationData":[OSD([subQ0])]})])],"derivedFrom":makeQuery(id+"F1.opExtrude","SWEPT_FACE",FACE,{"disambiguationData":[OSD([subQ2])]})})]}),makeQuery(id+"F4.opFillet","BLEND_FACE",FACE,{"disambiguationData":[OSD([subQ0])]})],"blendedInto":[makeQuery(id+"F4.opFillet","BLEND_FACE",FACE,{"disambiguationData":[OSD([subQ0])]})]});}
            var Q33;
            {var subQ0=sQuery(id+"F2.wireOp",EDGE,"E2");var subQ3=sQuery(id+"F0.wireOp",EDGE,"E0");var subQ5=makeQuery(id+"F3.opExtrude","SWEPT_FACE",FACE,{"disambiguationData":[OSD([subQ0])]});var subQ6=makeQuery(id+"F1.opExtrude","SWEPT_FACE",FACE,{"disambiguationData":[OSD([subQ3])]});Q33=makeQuery(id+"F5.opFillet","BLEND_EDGE",EDGE,{"blendedFrom":[makeQuery(id+"F3.boolean.opBoolean","SPLIT",EDGE,{"disambiguationData":[TD([subQ5])],"derivedFrom":makeQuery(id+"F1.opExtrude","CAP_EDGE",EDGE,{"disambiguationData":[OSD([subQ3])],"isStart":false})}),makeQuery(id+"F4.opFillet","BLEND_EDGE",EDGE,{"disambiguationData":[OD(1.0)],"blendedFrom":[makeQuery(id+"F3.opExtrude","CAP_EDGE",EDGE,{"disambiguationData":[OSD([subQ0])],"isStart":false}),makeQuery(id+"F3.boolean.opBoolean","SPLIT",FACE,{"disambiguationData":[TD([subQ5])],"derivedFrom":subQ6})],"blendedInto":[makeQuery(id+"F3.boolean.opBoolean","SPLIT",FACE,{"disambiguationData":[TD([subQ5])],"derivedFrom":subQ6})]})],"blendedInto":[]});}
            var Q34;
            {var subQ0=sQuery(id+"F2.wireOp",EDGE,"E2");var subQ1=sQuery(id+"F2.wireOp",EDGE,"E1");var subQ2=makeQuery(id+"F3.opExtrude","CAP_FACE",FACE,{"disambiguationData":[OSD([subQ1,subQ0])],"isStart":false});var subQ3=sQuery(id+"F0.wireOp",EDGE,"E0");var subQ4=makeQuery(id+"F1.opExtrude","CAP_FACE",FACE,{"disambiguationData":[OSD([subQ3])],"isStart":false});Q34=makeQuery(id+"F5.opFillet","BLEND_EDGE",EDGE,{"blendedFrom":[makeQuery(id+"F4.opFillet","BLEND_EDGE",EDGE,{"disambiguationData":[OD(0.0)],"blendedFrom":[makeQuery(id+"F3.opExtrude","CAP_EDGE",EDGE,{"disambiguationData":[OSD([subQ0])],"isStart":false}),makeQuery(id+"F3.boolean.opBoolean","SPLIT",FACE,{"disambiguationData":[TD([makeQuery(id+"F3.opExtrude","SWEPT_FACE",FACE,{"disambiguationData":[OSD([subQ0])]})])],"derivedFrom":makeQuery(id+"F1.opExtrude","SWEPT_FACE",FACE,{"disambiguationData":[OSD([subQ3])]})})],"blendedInto":[makeQuery(id+"F3.boolean.opBoolean","SPLIT",FACE,{"disambiguationData":[TD([makeQuery(id+"F3.opExtrude","SWEPT_FACE",FACE,{"disambiguationData":[OSD([subQ0])]})])],"derivedFrom":makeQuery(id+"F1.opExtrude","SWEPT_FACE",FACE,{"disambiguationData":[OSD([subQ3])]})})]}),makeQuery(id+"F3.boolean.opBoolean","MERGE",FACE,{"derivedFrom":[subQ4,subQ2]})],"blendedInto":[makeQuery(id+"F3.boolean.opBoolean","MERGE",FACE,{"derivedFrom":[subQ4,subQ2]})]});}
            var Q35;
            {var subQ0=sQuery(id+"F2.wireOp",EDGE,"E1");var subQ1=makeQuery(id+"F3.opExtrude","CAP_FACE",FACE,{"disambiguationData":[OSD([subQ0,sQuery(id+"F2.wireOp",EDGE,"E2")])],"isStart":true});var subQ2=sQuery(id+"F0.wireOp",EDGE,"E0");var subQ3=makeQuery(id+"F1.opExtrude","CAP_FACE",FACE,{"disambiguationData":[OSD([subQ2])],"isStart":true});var subQ4=makeQuery(id+"F3.opExtrude","SWEPT_FACE",FACE,{"disambiguationData":[OSD([subQ0])]});var subQ5=makeQuery(id+"F1.opExtrude","SWEPT_FACE",FACE,{"disambiguationData":[OSD([subQ2])]});Q35=makeQuery(id+"F6.opFillet","BLEND_EDGE",EDGE,{"blendedFrom":[makeQuery(id+"F3.boolean.opBoolean","SPLIT",EDGE,{"disambiguationData":[TD([subQ4])],"derivedFrom":makeQuery(id+"F1.opExtrude","CAP_EDGE",EDGE,{"disambiguationData":[OSD([subQ2])],"isStart":true})}),makeQuery(id+"F5.opFillet","BLEND_EDGE",EDGE,{"blendedFrom":[makeQuery(id+"F3.boolean.opBoolean","INTERSECT",EDGE,{"disambiguationData":[OD(1.0)],"derivedFrom":[subQ5,subQ4]}),makeQuery(id+"F3.boolean.opBoolean","MERGE",FACE,{"derivedFrom":[subQ3,subQ1]})],"blendedInto":[makeQuery(id+"F3.boolean.opBoolean","MERGE",FACE,{"derivedFrom":[subQ3,subQ1]})]})],"blendedInto":[]});}
            var Q36;
            {var subQ0=sQuery(id+"F2.wireOp",EDGE,"E1");var subQ1=sQuery(id+"F0.wireOp",EDGE,"E0");var subQ2=makeQuery(id+"F3.boolean.opBoolean","INTERSECT",EDGE,{"disambiguationData":[OD(0.0)],"derivedFrom":[makeQuery(id+"F1.opExtrude","SWEPT_FACE",FACE,{"disambiguationData":[OSD([subQ1])]}),makeQuery(id+"F3.opExtrude","SWEPT_FACE",FACE,{"disambiguationData":[OSD([subQ0])]})]});Q36=makeQuery(id+"F6.opFillet","BLEND_EDGE",EDGE,{"blendedFrom":[makeQuery(id+"F5.opFillet","BLEND_EDGE",EDGE,{"blendedFrom":[subQ2,makeQuery(id+"F3.boolean.opBoolean","MERGE",FACE,{"derivedFrom":[makeQuery(id+"F1.opExtrude","CAP_FACE",FACE,{"disambiguationData":[OSD([subQ1])],"isStart":true}),makeQuery(id+"F3.opExtrude","CAP_FACE",FACE,{"disambiguationData":[OSD([subQ0,sQuery(id+"F2.wireOp",EDGE,"E2")])],"isStart":true})]})],"blendedInto":[makeQuery(id+"F3.boolean.opBoolean","MERGE",FACE,{"derivedFrom":[makeQuery(id+"F1.opExtrude","CAP_FACE",FACE,{"disambiguationData":[OSD([subQ1])],"isStart":true}),makeQuery(id+"F3.opExtrude","CAP_FACE",FACE,{"disambiguationData":[OSD([subQ0,sQuery(id+"F2.wireOp",EDGE,"E2")])],"isStart":true})]})]}),makeQuery(id+"F5.opFillet","BLEND_FACE",FACE,{"disambiguationData":[OSD([subQ1,subQ0]),TDD([subQ2])]})],"blendedInto":[makeQuery(id+"F5.opFillet","BLEND_FACE",FACE,{"disambiguationData":[OSD([subQ1,subQ0]),TDD([subQ2])]})]});}
            var Q37;
            {var subQ0=sQuery(id+"F2.wireOp",EDGE,"E1");var subQ1=sQuery(id+"F0.wireOp",EDGE,"E0");var subQ2=makeQuery(id+"F3.boolean.opBoolean","MERGE",FACE,{"derivedFrom":[makeQuery(id+"F1.opExtrude","CAP_FACE",FACE,{"disambiguationData":[OSD([subQ1])],"isStart":true}),makeQuery(id+"F3.opExtrude","CAP_FACE",FACE,{"disambiguationData":[OSD([subQ0,sQuery(id+"F2.wireOp",EDGE,"E2")])],"isStart":true})]});Q37=makeQuery(id+"F6.opFillet","BLEND_EDGE",EDGE,{"blendedFrom":[makeQuery(id+"F5.opFillet","BLEND_EDGE",EDGE,{"blendedFrom":[makeQuery(id+"F3.boolean.opBoolean","INTERSECT",EDGE,{"disambiguationData":[OD(0.0)],"derivedFrom":[makeQuery(id+"F1.opExtrude","SWEPT_FACE",FACE,{"disambiguationData":[OSD([subQ1])]}),makeQuery(id+"F3.opExtrude","SWEPT_FACE",FACE,{"disambiguationData":[OSD([subQ0])]})]}),subQ2],"blendedInto":[subQ2]}),subQ2],"blendedInto":[subQ2]});}
            var Q38;
            {var subQ0=sQuery(id+"F2.wireOp",EDGE,"E1");var subQ1=sQuery(id+"F0.wireOp",EDGE,"E0");var subQ2=makeQuery(id+"F3.boolean.opBoolean","INTERSECT",EDGE,{"disambiguationData":[OD(1.0)],"derivedFrom":[makeQuery(id+"F1.opExtrude","SWEPT_FACE",FACE,{"disambiguationData":[OSD([subQ1])]}),makeQuery(id+"F3.opExtrude","SWEPT_FACE",FACE,{"disambiguationData":[OSD([subQ0])]})]});Q38=makeQuery(id+"F6.opFillet","BLEND_EDGE",EDGE,{"blendedFrom":[makeQuery(id+"F5.opFillet","BLEND_EDGE",EDGE,{"blendedFrom":[subQ2,makeQuery(id+"F3.boolean.opBoolean","MERGE",FACE,{"derivedFrom":[makeQuery(id+"F1.opExtrude","CAP_FACE",FACE,{"disambiguationData":[OSD([subQ1])],"isStart":true}),makeQuery(id+"F3.opExtrude","CAP_FACE",FACE,{"disambiguationData":[OSD([subQ0,sQuery(id+"F2.wireOp",EDGE,"E2")])],"isStart":true})]})],"blendedInto":[makeQuery(id+"F3.boolean.opBoolean","MERGE",FACE,{"derivedFrom":[makeQuery(id+"F1.opExtrude","CAP_FACE",FACE,{"disambiguationData":[OSD([subQ1])],"isStart":true}),makeQuery(id+"F3.opExtrude","CAP_FACE",FACE,{"disambiguationData":[OSD([subQ0,sQuery(id+"F2.wireOp",EDGE,"E2")])],"isStart":true})]})]}),makeQuery(id+"F5.opFillet","BLEND_FACE",FACE,{"disambiguationData":[OSD([subQ1,subQ0]),TDD([subQ2])]})],"blendedInto":[makeQuery(id+"F5.opFillet","BLEND_FACE",FACE,{"disambiguationData":[OSD([subQ1,subQ0]),TDD([subQ2])]})]});}
            var Q39;
            {var subQ0=sQuery(id+"F2.wireOp",EDGE,"E1");var subQ1=sQuery(id+"F0.wireOp",EDGE,"E0");var subQ2=makeQuery(id+"F3.boolean.opBoolean","MERGE",FACE,{"derivedFrom":[makeQuery(id+"F1.opExtrude","CAP_FACE",FACE,{"disambiguationData":[OSD([subQ1])],"isStart":true}),makeQuery(id+"F3.opExtrude","CAP_FACE",FACE,{"disambiguationData":[OSD([subQ0,sQuery(id+"F2.wireOp",EDGE,"E2")])],"isStart":true})]});Q39=makeQuery(id+"F6.opFillet","BLEND_EDGE",EDGE,{"blendedFrom":[makeQuery(id+"F5.opFillet","BLEND_EDGE",EDGE,{"blendedFrom":[makeQuery(id+"F3.boolean.opBoolean","INTERSECT",EDGE,{"disambiguationData":[OD(1.0)],"derivedFrom":[makeQuery(id+"F1.opExtrude","SWEPT_FACE",FACE,{"disambiguationData":[OSD([subQ1])]}),makeQuery(id+"F3.opExtrude","SWEPT_FACE",FACE,{"disambiguationData":[OSD([subQ0])]})]}),subQ2],"blendedInto":[subQ2]}),subQ2],"blendedInto":[subQ2]});}
            var Q40;
            {var subQ1=sQuery(id+"F2.wireOp",EDGE,"E1");var subQ2=sQuery(id+"F0.wireOp",EDGE,"E0");var subQ3=makeQuery(id+"F3.opExtrude","SWEPT_FACE",FACE,{"disambiguationData":[OSD([subQ1])]});var subQ4=makeQuery(id+"F1.opExtrude","SWEPT_FACE",FACE,{"disambiguationData":[OSD([subQ2])]});Q40=makeQuery(id+"F5.opFillet","BLEND_EDGE",EDGE,{"blendedFrom":[makeQuery(id+"F3.boolean.opBoolean","INTERSECT",EDGE,{"disambiguationData":[OD(0.0)],"derivedFrom":[subQ4,subQ3]}),makeQuery(id+"F3.boolean.opBoolean","SPLIT",FACE,{"disambiguationData":[TD([subQ3])],"derivedFrom":subQ4})],"blendedInto":[makeQuery(id+"F3.boolean.opBoolean","SPLIT",FACE,{"disambiguationData":[TD([subQ3])],"derivedFrom":subQ4})]});}
            var Q41;
            {var subQ0=makeQuery(id+"F3.opExtrude","SWEPT_FACE",FACE,{"disambiguationData":[OSD([sQuery(id+"F2.wireOp",EDGE,"E2")])]});var subQ1=makeQuery(id+"F1.opExtrude","SWEPT_FACE",FACE,{"disambiguationData":[OSD([sQuery(id+"F0.wireOp",EDGE,"E0")])]});Q41=makeQuery(id+"F5.opFillet","BLEND_EDGE",EDGE,{"blendedFrom":[makeQuery(id+"F3.boolean.opBoolean","INTERSECT",VERTEX,{"disambiguationData":[OD(1.0)],"derivedFrom":[subQ1,subQ0]}),makeQuery(id+"F3.boolean.opBoolean","INTERSECT",EDGE,{"disambiguationData":[OD(1.0)],"derivedFrom":[subQ1,subQ0]})],"blendedInto":[]});}
            var Q42;
            {var subQ0=sQuery(id+"F2.wireOp",EDGE,"E2");var subQ1=sQuery(id+"F0.wireOp",EDGE,"E0");Q42=makeQuery(id+"F5.opFillet","BLEND_EDGE",EDGE,{"blendedFrom":[makeQuery(id+"F3.boolean.opBoolean","INTERSECT",VERTEX,{"disambiguationData":[OD(1.0)],"derivedFrom":[makeQuery(id+"F1.opExtrude","SWEPT_FACE",FACE,{"disambiguationData":[OSD([subQ1])]}),makeQuery(id+"F3.opExtrude","SWEPT_FACE",FACE,{"disambiguationData":[OSD([subQ0])]})]}),makeQuery(id+"F3.boolean.opBoolean","MERGE",FACE,{"derivedFrom":[makeQuery(id+"F1.opExtrude","CAP_FACE",FACE,{"disambiguationData":[OSD([subQ1])],"isStart":true}),makeQuery(id+"F3.opExtrude","CAP_FACE",FACE,{"disambiguationData":[OSD([sQuery(id+"F2.wireOp",EDGE,"E1"),subQ0])],"isStart":true})]})],"blendedInto":[makeQuery(id+"F3.boolean.opBoolean","MERGE",FACE,{"derivedFrom":[makeQuery(id+"F1.opExtrude","CAP_FACE",FACE,{"disambiguationData":[OSD([subQ1])],"isStart":true}),makeQuery(id+"F3.opExtrude","CAP_FACE",FACE,{"disambiguationData":[OSD([sQuery(id+"F2.wireOp",EDGE,"E1"),subQ0])],"isStart":true})]})]});}
            var Q43;
            {var subQ0=sQuery(id+"F2.wireOp",EDGE,"E2");Q43=makeQuery(id+"F5.opFillet","BLEND_EDGE",EDGE,{"blendedFrom":[makeQuery(id+"F3.boolean.opBoolean","INTERSECT",VERTEX,{"disambiguationData":[OD(1.0)],"derivedFrom":[makeQuery(id+"F1.opExtrude","SWEPT_FACE",FACE,{"disambiguationData":[OSD([sQuery(id+"F0.wireOp",EDGE,"E0")])]}),makeQuery(id+"F3.opExtrude","SWEPT_FACE",FACE,{"disambiguationData":[OSD([subQ0])]})]}),makeQuery(id+"F3.opExtrude","CAP_EDGE",EDGE,{"disambiguationData":[OSD([subQ0])],"isStart":true})],"blendedInto":[]});}
            var Q44;
            {var subQ0=sQuery(id+"F0.wireOp",EDGE,"E0");var subQ1=makeQuery(id+"F1.opExtrude","SWEPT_FACE",FACE,{"disambiguationData":[OSD([subQ0])]});var subQ2=sQuery(id+"F2.wireOp",EDGE,"E2");var subQ3=makeQuery(id+"F3.opExtrude","SWEPT_FACE",FACE,{"disambiguationData":[OSD([subQ2])]});Q44=makeQuery(id+"F5.opFillet","BLEND_EDGE",EDGE,{"blendedFrom":[makeQuery(id+"F3.boolean.opBoolean","INTERSECT",VERTEX,{"disambiguationData":[OD(1.0)],"derivedFrom":[subQ1,subQ3]}),makeQuery(id+"F3.boolean.opBoolean","SPLIT",EDGE,{"disambiguationData":[TD([subQ3])],"derivedFrom":makeQuery(id+"F1.opExtrude","CAP_EDGE",EDGE,{"disambiguationData":[OSD([subQ0])],"isStart":true})})],"blendedInto":[]});}
            fillet(context, id + "F7", {"entities" : qUnion([Q0, Q1, Q2, Q3, Q4, Q5, Q6, Q7, Q8, Q9, Q10, Q11, Q12, Q13, Q14, Q15, Q16, Q17, Q18, Q19, Q20, Q21, Q22, Q23, Q24, Q25, Q26, Q27, Q28, Q29, Q30, Q31, Q32, Q33, Q34, Q35, Q36, Q37, Q38, Q39, Q40, Q41, Q42, Q43, Q44]), "radius" : 20.32 * mm, "tangentPropagation" : true, "allowEdgeOverflow" : false});
        }
    });
